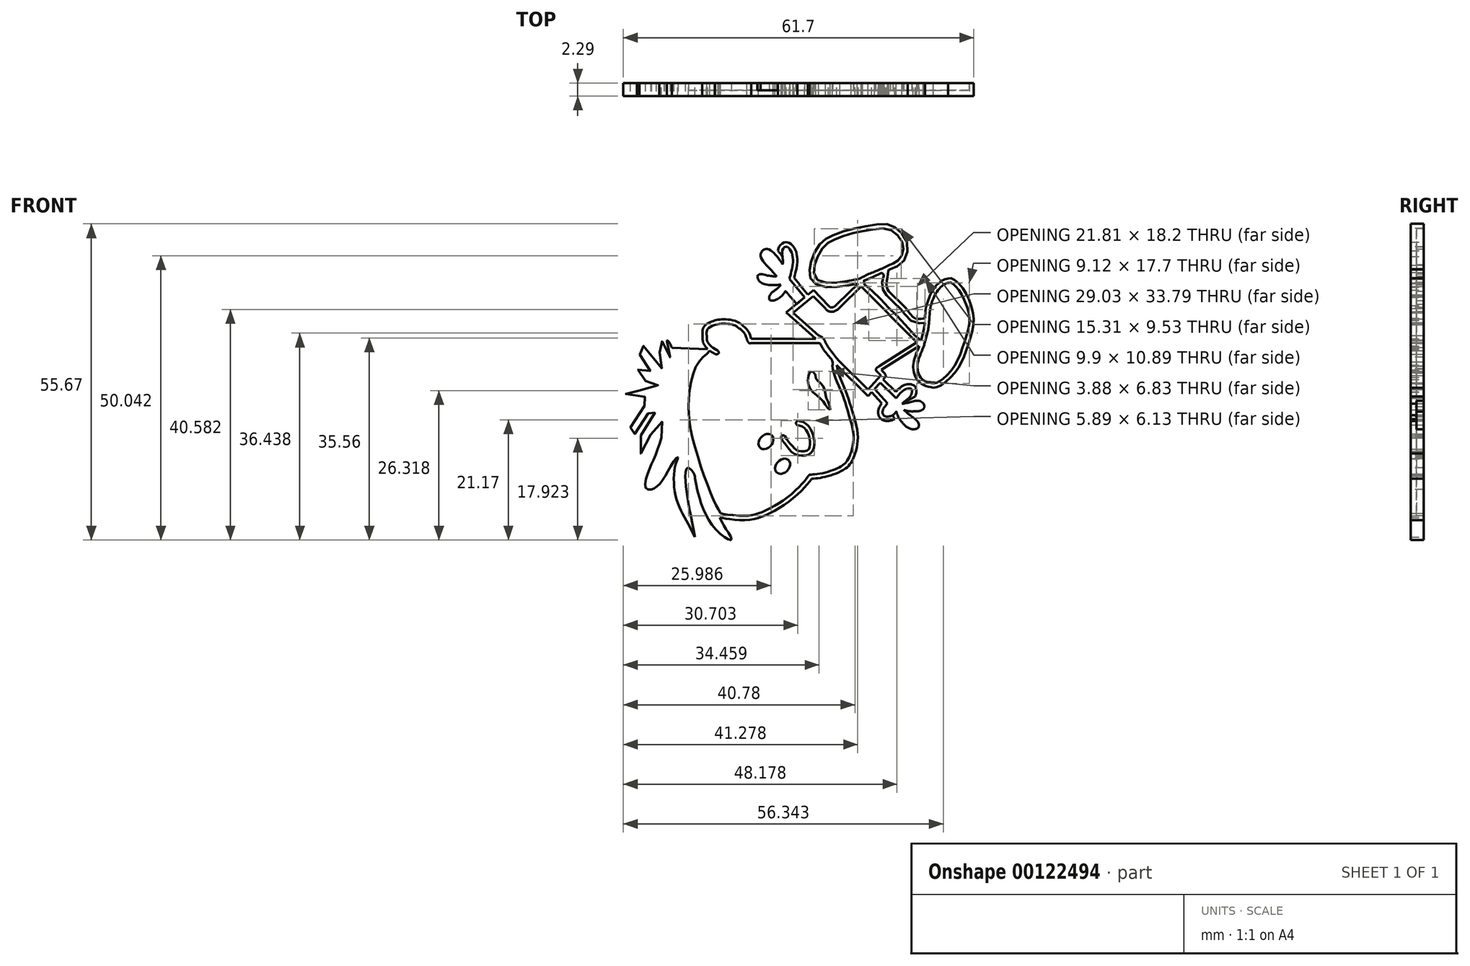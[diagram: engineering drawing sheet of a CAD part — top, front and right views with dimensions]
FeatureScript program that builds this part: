
annotation { "Feature Type Name" : "Feature", "Feature Type Description" : "" }
export const myFeature = defineFeature(function(context is Context, id is Id, definition is map)
    precondition{}
    {
        {
            var Q0;
            Q0=qCreatedBy(makeId("Front.planeOp"),FACE);
            var sketch = newSketch(context, id + "F0", { "sketchPlane" : qUnion([Q0])});
            skLineSegment(sketch, "E0.bottom", {"start": v(-35.67, 28.6) * mm, "end": v(40.53, 28.6) * mm});
            skLineSegment(sketch, "E0.top", {"start": v(-35.67, -29.82) * mm, "end": v(40.53, -29.82) * mm});
            skLineSegment(sketch, "E0.left", {"start": v(-35.67, 28.6) * mm, "end": v(-35.67, -29.82) * mm});
            skLineSegment(sketch, "E0.right", {"start": v(40.53, 28.6) * mm, "end": v(40.53, -29.82) * mm});
            skFitSpline(sketch, "E1", {"points": [v(2.5, -18.66) * mm, v(1.1, -20.33) * mm, v(-2.3, -23.23) * mm, v(-5.73, -25.1) * mm, v(-8.32, -25.86) * mm, v(-12.02, -25.75) * mm, v(-13.66, -25.48) * mm], "startDerivative": vector(-8.55, -11.05) * mm, "endDerivative": vector(-11.53, 2.21) * mm});
            skFitSpline(sketch, "E2.0", {"points": [v(1.9, -18.2) * mm, v(1.73, -18.42) * mm, v(1.47, -18.76) * mm, v(1.08, -19.22) * mm, v(0.75, -19.6) * mm, v(0.38, -19.99) * mm, v(-0.2, -20.56) * mm, v(-1.04, -21.32) * mm, v(-1.96, -22.06) * mm, v(-2.71, -22.6) * mm, v(-3.46, -23.1) * mm, v(-4.4, -23.63) * mm, v(-5.3, -24.08) * mm, v(-6, -24.39) * mm, v(-6.48, -24.6) * mm, v(-6.93, -24.77) * mm, v(-7.37, -24.91) * mm, v(-7.83, -25.02) * mm, v(-8.32, -25.1) * mm, v(-8.88, -25.15) * mm, v(-9.7, -25.16) * mm, v(-10.78, -25.12) * mm, v(-11.96, -25) * mm, v(-12.81, -24.87) * mm, v(-13.28, -24.78) * mm, v(-13.52, -24.73) * mm]});
            skFitSpline(sketch, "E3", {"points": [v(-13.66, -25.48) * mm, v(-12.8, -27.15) * mm, v(-11.63, -29.37) * mm, v(-14.37, -27.58) * mm, v(-17.37, -21.62) * mm, v(-18.02, -18.58) * mm], "startDerivative": vector(4.17, -9.52) * mm, "endDerivative": vector(-2.4, 14.14) * mm});
            skFitSpline(sketch, "E4", {"points": [v(-18.02, -18.58) * mm, v(-18.37, -17.5) * mm, v(-19.41, -16.75) * mm, v(-19.59, -20.54) * mm, v(-18.72, -25.45) * mm, v(-18.02, -28.89) * mm], "startDerivative": vector(-1.13, 8.11) * mm, "endDerivative": vector(2.94, -14.74) * mm});
            skFitSpline(sketch, "E5", {"points": [v(-18.02, -28.89) * mm, v(-19.98, -25.28) * mm, v(-21.6, -21.1) * mm, v(-21.55, -16.45) * mm, v(-21.07, -15.14) * mm], "startDerivative": vector(-7.28, 13.23) * mm, "endDerivative": vector(3.3, 6.7) * mm});
            skFitSpline(sketch, "E6", {"points": [v(-21.07, -15.14) * mm, v(-21.07, -14.86) * mm, v(-21.75, -15.5) * mm, v(-23.44, -18.41) * mm, v(-24.73, -20) * mm, v(-25.83, -20.55) * mm, v(-26.73, -20.25) * mm, v(-26.38, -17.7) * mm, v(-25.28, -15.14) * mm, v(-23.94, -11.4) * mm], "startDerivative": vector(1.52, 8.73) * mm, "endDerivative": vector(8.18, 24.32) * mm});
            skFitSpline(sketch, "E7", {"points": [v(-23.94, -11.4) * mm, v(-23.54, -10.35) * mm, v(-23.94, -8.56) * mm, v(-25.18, -9.9) * mm, v(-26.38, -11.85) * mm, v(-27.63, -14.2) * mm, v(-27.98, -13.2) * mm, v(-26.83, -9.5) * mm, v(-24.93, -6.56) * mm, v(-25.13, -6) * mm, v(-26.78, -7.86) * mm, v(-28.63, -10.7) * mm, v(-29.28, -11.4) * mm, v(-29.38, -9.5) * mm, v(-27.33, -6.16) * mm, v(-25.73, -4.36) * mm, v(-27.3, -4.27) * mm, v(-29.38, -4.07) * mm, v(-30.66, -3.33) * mm, v(-27.98, -3.13) * mm, v(-25.43, -2.66) * mm, v(-24.38, -1.85) * mm, v(-26.03, -1.65) * mm, v(-27.7, -0.51) * mm, v(-28.24, 0.56) * mm, v(-26.9, 0.1) * mm, v(-25.9, 0.02) * mm, v(-26.9, 1.77) * mm, v(-27.78, 3.44) * mm, v(-27.57, 5.32) * mm, v(-26.23, 3.18) * mm, v(-23.53, 0.79) * mm, v(-24.18, 3.23) * mm, v(-24.21, 4.8) * mm, v(-23.94, 5.7) * mm, v(-23.47, 4.16) * mm, v(-22.45, 2.75) * mm, v(-22.6, 3.68) * mm, v(-22.96, 5.39) * mm], "startDerivative": vector(25.66, 39.72) * mm, "endDerivative": vector(-0.87, 29.22) * mm});
            skFitSpline(sketch, "E8", {"points": [v(-14.36, 3.25) * mm, v(-15.42, 3.88) * mm, v(-16.03, 4.43) * mm, v(-16.57, 5.22) * mm, v(-16.72, 6.25) * mm, v(-16.63, 7.79) * mm, v(-15.75, 8.76) * mm, v(-14.54, 9.24) * mm], "startDerivative": vector(-7.8, 4.34) * mm, "endDerivative": vector(8.24, 2.58) * mm});
            skFitSpline(sketch, "E9", {"points": [v(-14.54, 9.24) * mm, v(-13.74, 9.38) * mm, v(-12.47, 9.4) * mm, v(-10.85, 9.1) * mm, v(-9.37, 8.1) * mm, v(-8.6, 7.23) * mm, v(-8.27, 6.45) * mm, v(-8.15, 6) * mm], "startDerivative": vector(6.15, 1.3) * mm, "endDerivative": vector(1.17, -4.4) * mm});
            skFitSpline(sketch, "E10", {"points": [v(-13.52, -24.73) * mm, v(-15.03, -21.77) * mm, v(-18.32, -12.1) * mm, v(-19.17, -4.98) * mm, v(-17.47, 1.8) * mm, v(-15.42, 3.88) * mm], "startDerivative": vector(-9.54, 15.92) * mm, "endDerivative": vector(10.17, 11.75) * mm});
            skFitSpline(sketch, "E11", {"points": [v(-22.96, 5.39) * mm, v(-22.96, 5.68) * mm, v(-22.7, 5.55) * mm, v(-22.12, 4.42) * mm], "startDerivative": vector(-0.27, 1.56) * mm, "endDerivative": vector(1.09, -2.65) * mm});
            skLineSegment(sketch, "E12", {"start": v(-22.12, 4.42) * mm, "end": v(-15.8, 4.2) * mm});
            skFitSpline(sketch, "E13.0", {"points": [v(-14.38, 8.5) * mm, v(-14.26, 8.52) * mm, v(-14.01, 8.58) * mm, v(-13.66, 8.63) * mm, v(-13.23, 8.66) * mm, v(-12.74, 8.66) * mm, v(-12.2, 8.64) * mm, v(-11.78, 8.59) * mm, v(-11.47, 8.51) * mm, v(-11.24, 8.44) * mm, v(-11.03, 8.35) * mm, v(-10.8, 8.24) * mm, v(-10.58, 8.1) * mm, v(-10.36, 7.94) * mm, v(-10.14, 7.76) * mm, v(-9.94, 7.59) * mm, v(-9.74, 7.41) * mm, v(-9.52, 7.2) * mm, v(-9.36, 7.01) * mm, v(-9.25, 6.85) * mm, v(-9.18, 6.71) * mm, v(-9.11, 6.56) * mm, v(-9.06, 6.4) * mm, v(-9, 6.24) * mm, v(-8.95, 6.03) * mm, v(-8.91, 5.9) * mm, v(-8.89, 5.81) * mm]});
            skFitSpline(sketch, "E13.1", {"points": [v(-14, 3.91) * mm, v(-14.15, 4) * mm, v(-14.47, 4.18) * mm, v(-14.81, 4.39) * mm, v(-15.02, 4.53) * mm, v(-15.2, 4.67) * mm, v(-15.35, 4.82) * mm, v(-15.53, 5.01) * mm, v(-15.65, 5.16) * mm, v(-15.76, 5.3) * mm, v(-15.82, 5.4) * mm, v(-15.86, 5.48) * mm, v(-15.88, 5.54) * mm, v(-15.9, 5.64) * mm, v(-15.93, 5.8) * mm, v(-15.94, 5.98) * mm, v(-15.95, 6.14) * mm, v(-15.96, 6.28) * mm, v(-15.97, 6.42) * mm, v(-15.98, 6.61) * mm, v(-16, 6.84) * mm, v(-15.99, 7.1) * mm, v(-15.97, 7.32) * mm, v(-15.94, 7.47) * mm, v(-15.9, 7.55) * mm, v(-15.87, 7.63) * mm, v(-15.8, 7.74) * mm, v(-15.7, 7.86) * mm, v(-15.51, 8.02) * mm, v(-15.22, 8.2) * mm, v(-14.81, 8.36) * mm, v(-14.49, 8.46) * mm, v(-14.32, 8.52) * mm]});
            skFitSpline(sketch, "E14", {"points": [v(-14.36, 3.25) * mm, v(-13.86, 3.45) * mm, v(-14, 3.91) * mm], "startDerivative": vector(1.3, 0.25) * mm, "endDerivative": vector(-0.58, 1.09) * mm});
            skLineSegment(sketch, "E15", {"start": v(-8.15, 6) * mm, "end": v(3.2, 6) * mm});
            skLineSegment(sketch, "E16.0", {"start": v(-8.15, 5.25) * mm, "end": v(3.2, 5.25) * mm});
            skFitSpline(sketch, "E17", {"points": [v(-8.15, 5.25) * mm, v(-8.51, 5.25) * mm, v(-8.89, 5.81) * mm], "startDerivative": vector(-0.9, -0.2) * mm, "endDerivative": vector(-0.59, 1.26) * mm});
            skFitSpline(sketch, "E18", {"points": [v(2.5, -18.66) * mm, v(4.7, -18.35) * mm, v(7.9, -17.2) * mm, v(9.41, -15.84) * mm, v(10.17, -14.2) * mm], "startDerivative": vector(8.36, 0.78) * mm, "endDerivative": vector(2.95, 7.75) * mm});
            skFitSpline(sketch, "E19", {"points": [v(10.17, -14.2) * mm, v(10.55, -12.5) * mm, v(10.55, -10.21) * mm, v(9.56, -6.45) * mm, v(8.65, -3.6) * mm, v(7.33, -0.37) * mm, v(6.91, 1.37) * mm], "startDerivative": vector(3.2, 12.34) * mm, "endDerivative": vector(-2.07, 11.63) * mm});
            skFitSpline(sketch, "E20.0", {"points": [v(2.44, -17.9) * mm, v(2.78, -17.87) * mm, v(3.46, -17.8) * mm, v(4.55, -17.62) * mm, v(5.67, -17.31) * mm, v(6.54, -17) * mm, v(7.15, -16.74) * mm, v(7.67, -16.47) * mm, v(8.07, -16.19) * mm, v(8.4, -15.9) * mm, v(8.67, -15.58) * mm, v(8.9, -15.24) * mm, v(9.16, -14.72) * mm, v(9.34, -14.26) * mm, v(9.46, -13.93) * mm]});
            skFitSpline(sketch, "E21", {"points": [v(1.9, -18.2) * mm, v(2.11, -17.95) * mm, v(2.44, -17.9) * mm], "startDerivative": vector(0.36, 0.59) * mm, "endDerivative": vector(0.7, 0) * mm});
            skFitSpline(sketch, "E22.0", {"points": [v(9.44, -14.01) * mm, v(9.5, -13.75) * mm, v(9.63, -13.25) * mm, v(9.79, -12.5) * mm, v(9.88, -11.76) * mm, v(9.89, -11.09) * mm, v(9.83, -10.48) * mm, v(9.72, -9.82) * mm, v(9.5, -8.87) * mm, v(9.14, -7.68) * mm, v(8.79, -6.53) * mm, v(8.5, -5.52) * mm, v(8.2, -4.59) * mm, v(7.85, -3.63) * mm, v(7.39, -2.54) * mm, v(7, -1.62) * mm, v(6.72, -0.92) * mm, v(6.48, -0.25) * mm, v(6.3, 0.5) * mm, v(6.2, 1) * mm, v(6.16, 1.24) * mm]});
            skFitSpline(sketch, "E23", {"points": [v(-0.07, -9.19) * mm, v(0.93, -9.47) * mm, v(1.73, -10.4) * mm, v(2.17, -11.84) * mm, v(2.17, -12.96) * mm, v(1.8, -13.6) * mm, v(0.54, -13.8) * mm, v(-0.29, -13.5) * mm, v(-1.22, -12.51) * mm, v(-1.89, -11.65) * mm, v(-2.24, -11.07) * mm], "startDerivative": vector(10.6, -1.7) * mm, "endDerivative": vector(-4.01, 7.06) * mm});
            skFitSpline(sketch, "E24.0", {"points": [v(0.06, -8.43) * mm, v(0.17, -8.45) * mm, v(0.4, -8.49) * mm, v(0.74, -8.57) * mm, v(1.03, -8.67) * mm, v(1.25, -8.78) * mm, v(1.47, -8.92) * mm, v(1.73, -9.12) * mm, v(2.01, -9.42) * mm, v(2.28, -9.82) * mm, v(2.5, -10.24) * mm, v(2.68, -10.68) * mm, v(2.81, -11.13) * mm, v(2.9, -11.58) * mm, v(2.97, -12.02) * mm, v(3, -12.44) * mm, v(2.97, -12.8) * mm, v(2.93, -13.06) * mm, v(2.87, -13.33) * mm, v(2.76, -13.64) * mm, v(2.55, -13.95) * mm, v(2.33, -14.16) * mm, v(2.07, -14.33) * mm, v(1.8, -14.43) * mm, v(1.55, -14.5) * mm, v(1.22, -14.55) * mm, v(0.9, -14.57) * mm, v(0.59, -14.56) * mm, v(0.3, -14.54) * mm, v(-0.07, -14.47) * mm, v(-0.5, -14.3) * mm, v(-0.88, -14.02) * mm, v(-1.2, -13.7) * mm, v(-1.5, -13.38) * mm, v(-1.75, -13.06) * mm, v(-2, -12.77) * mm, v(-2.22, -12.49) * mm, v(-2.43, -12.21) * mm, v(-2.68, -11.84) * mm, v(-2.82, -11.6) * mm, v(-2.9, -11.45) * mm]});
            skFitSpline(sketch, "E25", {"points": [v(-2.9, -11.45) * mm, v(-2.72, -11.01) * mm, v(-2.24, -11.07) * mm], "startDerivative": vector(0.22, 1.13) * mm, "endDerivative": vector(1.1, -0.37) * mm});
            skFitSpline(sketch, "E26", {"points": [v(-0.07, -9.19) * mm, v(-0.29, -8.79) * mm, v(0.06, -8.43) * mm], "startDerivative": vector(-0.73, 0.84) * mm, "endDerivative": vector(0.96, 0.67) * mm});
            skEllipse(sketch, "E27", {"center": v(-5.56, -12.08) * mm, "majorRadius": 1.5 * mm, "minorRadius": 1.13 * mm, "majorAxis": v(0.68, 0.73)});
            skEllipse(sketch, "E28", {"center": v(-2.61, -16.43) * mm, "majorRadius": 1.5 * mm, "minorRadius": 1.13 * mm, "majorAxis": v(0.68, 0.73)});
            skFitSpline(sketch, "E29", {"points": [v(5.74, -6.52) * mm, v(4.98, -5.77) * mm, v(4.5, -4.94) * mm, v(3.18, -3.8) * mm, v(2.09, -2.57) * mm, v(1.86, -1.17) * mm, v(2.31, 0.3) * mm, v(3.1, -0.16) * mm, v(3.25, -1.02) * mm, v(3.9, -1.63) * mm, v(4.72, -2.72) * mm, v(4.98, -4.03) * mm, v(5.4, -5.16) * mm, v(5.74, -6.52) * mm]});
            skLineSegment(sketch, "E30", {"start": v(6.91, 1.37) * mm, "end": v(12.43, -4.08) * mm});
            skFitSpline(sketch, "E31", {"points": [v(15.43, -0.8) * mm, v(15.55, -0.63) * mm, v(15.43, -0.21) * mm, v(14.79, 0.53) * mm], "startDerivative": vector(0.72, 0.68) * mm, "endDerivative": vector(-1.54, 1.65) * mm});
            skLineSegment(sketch, "E32", {"start": v(14.79, 0.53) * mm, "end": v(21.47, 4.75) * mm});
            skLineSegment(sketch, "E33", {"start": v(3.2, 6) * mm, "end": v(-1.96, 10.62) * mm});
            skLineSegment(sketch, "E34", {"start": v(-1.96, 10.62) * mm, "end": v(2.82, 14.57) * mm});
            skLineSegment(sketch, "E35", {"start": v(2.82, 14.57) * mm, "end": v(5.46, 11.87) * mm});
            skFitSpline(sketch, "E36", {"points": [v(5.46, 11.87) * mm, v(5.72, 11.59) * mm, v(6.25, 11.56) * mm, v(7.09, 12.2) * mm], "startDerivative": vector(0.83, -1.22) * mm, "endDerivative": vector(1.93, 1.9) * mm});
            skLineSegment(sketch, "E37", {"start": v(7.09, 12.2) * mm, "end": v(10.7, 15.76) * mm});
            skFitSpline(sketch, "E38", {"points": [v(6.16, 1.24) * mm, v(6.16, 2.04) * mm, v(5.3, 3.2) * mm, v(4.31, 4.55) * mm, v(3.95, 5.17) * mm, v(3.2, 5.25) * mm], "startDerivative": vector(0.79, 4.51) * mm, "endDerivative": vector(-5.08, -0.36) * mm});
            skFitSpline(sketch, "E39", {"points": [v(21.47, 4.75) * mm, v(20.57, 2.37) * mm, v(20.41, 0.46) * mm, v(21.47, -1.69) * mm, v(23.9, -2.6) * mm], "startDerivative": vector(-4.04, -9.6) * mm, "endDerivative": vector(10.28, -2.2) * mm});
            skFitSpline(sketch, "E40", {"points": [v(23.9, -2.6) * mm, v(25.03, -2.3) * mm, v(27.01, -0.78) * mm, v(28.68, 1.51) * mm, v(29.73, 4) * mm, v(30.74, 7.22) * mm, v(31.01, 9.9) * mm, v(30.12, 13.04) * mm, v(28.65, 15.5) * mm, v(27.17, 16.62) * mm, v(26.5, 16.62) * mm], "startDerivative": vector(14.92, 2.44) * mm, "endDerivative": vector(-11.36, -2.14) * mm});
            skFitSpline(sketch, "E41", {"points": [v(26.5, 16.62) * mm, v(25.51, 16.29) * mm, v(24.13, 15) * mm, v(23.26, 13.46) * mm, v(22.69, 11.7) * mm, v(22.46, 9.63) * mm], "startDerivative": vector(-6.17, -1.27) * mm, "endDerivative": vector(-0.6, -9.52) * mm});
            skFitSpline(sketch, "E42.0", {"points": [v(22.16, 4.46) * mm, v(22, 4.06) * mm, v(21.75, 3.47) * mm, v(21.47, 2.74) * mm, v(21.3, 2.23) * mm, v(21.19, 1.77) * mm, v(21.12, 1.34) * mm, v(21.11, 0.92) * mm, v(21.16, 0.47) * mm, v(21.29, -0.02) * mm, v(21.48, -0.5) * mm, v(21.7, -0.83) * mm, v(21.88, -1.04) * mm, v(22.03, -1.17) * mm, v(22.2, -1.3) * mm, v(22.46, -1.43) * mm, v(22.86, -1.59) * mm, v(23.43, -1.73) * mm, v(23.85, -1.82) * mm, v(24.06, -1.87) * mm]});
            skFitSpline(sketch, "E43.0", {"points": [v(26.66, 15.87) * mm, v(26.53, 15.85) * mm, v(26.3, 15.8) * mm, v(26.08, 15.72) * mm, v(25.9, 15.63) * mm, v(25.74, 15.53) * mm, v(25.57, 15.4) * mm, v(25.33, 15.2) * mm, v(25.02, 14.9) * mm, v(24.7, 14.49) * mm, v(24.43, 14.1) * mm, v(24.2, 13.67) * mm, v(24, 13.23) * mm, v(23.73, 12.59) * mm, v(23.51, 11.94) * mm, v(23.38, 11.28) * mm, v(23.28, 10.56) * mm, v(23.25, 9.98) * mm, v(23.22, 9.59) * mm]});
            skFitSpline(sketch, "E43.1", {"points": [v(23.78, -1.85) * mm, v(23.94, -1.83) * mm, v(24.15, -1.8) * mm, v(24.4, -1.73) * mm, v(24.6, -1.66) * mm, v(24.8, -1.57) * mm, v(25.04, -1.43) * mm, v(25.3, -1.26) * mm, v(25.67, -1) * mm, v(26.14, -0.59) * mm, v(26.67, -0.05) * mm, v(27.15, 0.53) * mm, v(27.58, 1.13) * mm, v(27.96, 1.76) * mm, v(28.39, 2.6) * mm, v(28.74, 3.49) * mm, v(29.11, 4.52) * mm, v(29.4, 5.33) * mm, v(29.66, 6.17) * mm, v(29.9, 6.99) * mm, v(30.1, 7.76) * mm, v(30.23, 8.47) * mm, v(30.3, 9.14) * mm, v(30.27, 9.81) * mm, v(30.16, 10.55) * mm, v(29.96, 11.32) * mm, v(29.69, 12.11) * mm, v(29.37, 12.88) * mm, v(29.03, 13.59) * mm, v(28.66, 14.22) * mm, v(28.32, 14.7) * mm, v(28.03, 15.04) * mm, v(27.8, 15.28) * mm, v(27.57, 15.5) * mm, v(27.35, 15.67) * mm, v(27.15, 15.8) * mm, v(27.02, 15.86) * mm, v(26.95, 15.89) * mm, v(26.91, 15.9) * mm, v(26.88, 15.9) * mm, v(26.8, 15.9) * mm, v(26.7, 15.88) * mm, v(26.65, 15.87) * mm]});
            skFitSpline(sketch, "E44", {"points": [v(22.46, 9.63) * mm, v(21.82, 9.53) * mm, v(20.66, 9.63) * mm, v(19.18, 11.25) * mm, v(17.62, 12.85) * mm, v(16.42, 14.01) * mm, v(15.86, 14.65) * mm, v(15.7, 15.7) * mm, v(15.94, 17.5) * mm, v(16.08, 18.18) * mm], "startDerivative": vector(-7.76, -0.9) * mm, "endDerivative": vector(1.85, 7.1) * mm});
            skFitSpline(sketch, "E45", {"points": [v(22.16, 4.46) * mm, v(22.4, 5.22) * mm, v(22.77, 6.54) * mm, v(23.08, 8.01) * mm, v(23.22, 9.59) * mm], "startDerivative": vector(1.02, 3.44) * mm, "endDerivative": vector(0.38, 5.72) * mm});
            skPoint(sketch, "E46", {"position": v(16.08, 18.94) * mm});
            skFitSpline(sketch, "E47", {"points": [v(16.08, 18.94) * mm, v(16.6, 19.17) * mm, v(17.33, 19.51) * mm, v(17.92, 19.97) * mm, v(18.48, 20.98) * mm, v(18.66, 22.2) * mm, v(18.18, 23.55) * mm, v(16.85, 24.9) * mm, v(15.26, 25.47) * mm, v(12.23, 25.1) * mm, v(9.96, 24.63) * mm, v(7.59, 23.94) * mm, v(5.86, 23.16) * mm, v(4.6, 22.22) * mm, v(3.4, 20.14) * mm, v(2.94, 18.54) * mm, v(3.13, 16.72) * mm, v(5.15, 15.88) * mm, v(7.91, 16.04) * mm, v(10.53, 16.5) * mm], "startDerivative": vector(16.63, 6.8) * mm, "endDerivative": vector(38.76, 9.66) * mm});
            skFitSpline(sketch, "E48.0", {"points": [v(16.37, 18.24) * mm, v(16.55, 18.3) * mm, v(16.82, 18.42) * mm, v(17.27, 18.62) * mm, v(17.62, 18.8) * mm, v(17.98, 19) * mm, v(18.35, 19.3) * mm, v(18.68, 19.69) * mm, v(18.95, 20.13) * mm, v(19.18, 20.62) * mm, v(19.34, 21.14) * mm, v(19.43, 21.68) * mm, v(19.43, 22.25) * mm, v(19.34, 22.82) * mm, v(19.15, 23.38) * mm, v(18.86, 23.92) * mm, v(18.49, 24.43) * mm, v(18.06, 24.9) * mm, v(17.66, 25.24) * mm, v(17.34, 25.49) * mm, v(17, 25.71) * mm, v(16.56, 25.96) * mm, v(16.05, 26.12) * mm, v(15.6, 26.2) * mm, v(15.14, 26.24) * mm, v(14.54, 26.23) * mm, v(13.8, 26.15) * mm, v(13.05, 26.03) * mm, v(12.34, 25.9) * mm, v(11.7, 25.77) * mm, v(10.91, 25.61) * mm, v(10.17, 25.46) * mm, v(9.37, 25.27) * mm, v(8.54, 25.06) * mm, v(7.7, 24.8) * mm, v(6.93, 24.51) * mm, v(6.39, 24.28) * mm, v(5.97, 24.08) * mm, v(5.66, 23.92) * mm, v(5.36, 23.76) * mm, v(4.97, 23.54) * mm, v(4.58, 23.26) * mm, v(4.27, 22.99) * mm, v(4.04, 22.75) * mm, v(3.83, 22.5) * mm, v(3.56, 22.12) * mm, v(3.26, 21.63) * mm, v(2.95, 21.02) * mm, v(2.68, 20.44) * mm, v(2.48, 19.9) * mm, v(2.32, 19.38) * mm, v(2.23, 18.94) * mm, v(2.17, 18.56) * mm, v(2.12, 18.15) * mm, v(2.1, 17.7) * mm, v(2.14, 17.23) * mm, v(2.22, 16.86) * mm, v(2.37, 16.5) * mm, v(2.6, 16.13) * mm, v(2.9, 15.85) * mm, v(3.34, 15.56) * mm, v(3.92, 15.32) * mm, v(4.66, 15.15) * mm, v(5.4, 15.08) * mm, v(6.11, 15.08) * mm, v(6.8, 15.13) * mm, v(7.48, 15.21) * mm, v(8.13, 15.3) * mm, v(8.78, 15.4) * mm, v(9.64, 15.53) * mm, v(10.3, 15.66) * mm, v(10.72, 15.76) * mm]});
            skFitSpline(sketch, "E49", {"points": [v(16.37, 18.24) * mm, v(16.08, 18.18) * mm], "startDerivative": vector(-0.29, -0.06) * mm, "endDerivative": vector(-0.29, -0.06) * mm});
            skFitSpline(sketch, "E50", {"points": [v(10.53, 16.5) * mm, v(12.05, 17.19) * mm, v(14.1, 18.04) * mm, v(16.08, 18.94) * mm], "startDerivative": vector(5.38, 1.13) * mm, "endDerivative": vector(5.42, 2.95) * mm});
            skLineSegment(sketch, "E51.0", {"start": v(14.38, 1.18) * mm, "end": v(21.03, 5.37) * mm});
            skLineSegment(sketch, "E52.1", {"start": v(12.4, -2.96) * mm, "end": v(14.68, -0.48) * mm});
            skLineSegment(sketch, "E52.2", {"start": v(7.46, 1.92) * mm, "end": v(12.4, -2.96) * mm});
            skPoint(sketch, "E53", {"position": v(14.24, 0.02) * mm});
            skFitSpline(sketch, "E54", {"points": [v(14.68, -0.48) * mm, v(14.51, -0.27) * mm, v(14.24, 0.02) * mm], "startDerivative": vector(-0.34, 0.46) * mm, "endDerivative": vector(-0.53, 0.53) * mm});
            skLineSegment(sketch, "E55.0", {"start": v(2.76, 13.53) * mm, "end": v(4.94, 11.3) * mm});
            skLineSegment(sketch, "E55.1", {"start": v(-0.79, 10.6) * mm, "end": v(2.76, 13.53) * mm});
            skLineSegment(sketch, "E55.2", {"start": v(3.7, 6.59) * mm, "end": v(-0.79, 10.6) * mm});
            skLineSegment(sketch, "E56.0", {"start": v(7.62, 11.67) * mm, "end": v(11.24, 15.24) * mm});
            skFitSpline(sketch, "E56.1", {"points": [v(4.84, 11.44) * mm, v(4.86, 11.42) * mm, v(4.9, 11.36) * mm, v(5, 11.23) * mm, v(5.12, 11.1) * mm, v(5.28, 10.97) * mm, v(5.43, 10.9) * mm, v(5.58, 10.83) * mm, v(5.77, 10.78) * mm, v(6, 10.76) * mm, v(6.25, 10.78) * mm, v(6.49, 10.84) * mm, v(6.71, 10.94) * mm, v(6.9, 11.05) * mm, v(7.12, 11.21) * mm, v(7.36, 11.42) * mm, v(7.53, 11.6) * mm, v(7.62, 11.67) * mm]});
            skLineSegment(sketch, "E57", {"start": v(21.03, 5.37) * mm, "end": v(11.24, 15.24) * mm});
            skFitSpline(sketch, "E58", {"points": [v(3.7, 6.59) * mm, v(4.44, 6.19) * mm, v(4.96, 5.31) * mm, v(5.56, 4.3) * mm, v(6.82, 2.72) * mm, v(7.46, 1.92) * mm], "startDerivative": vector(4.71, -1.76) * mm, "endDerivative": vector(3, -3.82) * mm});
            skFitSpline(sketch, "E59", {"points": [v(14.24, 0.02) * mm, v(13.8, 0.58) * mm, v(14.38, 1.18) * mm], "startDerivative": vector(-1.42, 1.19) * mm, "endDerivative": vector(1.67, 1.13) * mm});
            skFitSpline(sketch, "E60", {"points": [v(13.59, -2.81) * mm, v(15.84, -5.33) * mm], "startDerivative": vector(2.25, -2.52) * mm, "endDerivative": vector(2.25, -2.52) * mm});
            skFitSpline(sketch, "E61", {"points": [v(15.84, -5.33) * mm, v(15.53, -5.75) * mm, v(15.07, -6.45) * mm, v(15.1, -7.38) * mm, v(15.84, -7.7) * mm, v(16.93, -7.34) * mm, v(17.39, -6.76) * mm], "startDerivative": vector(-2.1, -3.07) * mm, "endDerivative": vector(2.28, 3.92) * mm});
            skFitSpline(sketch, "E62", {"points": [v(17.39, -6.76) * mm, v(17.82, -7.85) * mm, v(18.55, -8.85) * mm, v(19.79, -9.82) * mm, v(21.18, -9.7) * mm, v(21.3, -8.81) * mm, v(20.37, -7.85) * mm, v(18.7, -6.53) * mm], "startDerivative": vector(2.78, -8.47) * mm, "endDerivative": vector(-9.72, 7.75) * mm});
            skFitSpline(sketch, "E63", {"points": [v(18.7, -6.53) * mm, v(19.68, -6.76) * mm, v(20.9, -6.76) * mm, v(21.98, -6.53) * mm, v(22.36, -5.76) * mm, v(21.41, -4.92) * mm, v(19.96, -5.12) * mm, v(18.42, -5.43) * mm], "startDerivative": vector(7.2, -2.18) * mm, "endDerivative": vector(-9.43, -1.54) * mm});
            skFitSpline(sketch, "E64", {"points": [v(18.42, -5.43) * mm, v(19.09, -4.87) * mm, v(19.98, -3.97) * mm, v(20.09, -2.88) * mm, v(19.22, -2.82) * mm, v(18.04, -3.64) * mm, v(17.4, -4.46) * mm], "startDerivative": vector(4.15, 3.68) * mm, "endDerivative": vector(-3.44, -4.99) * mm});
            skFitSpline(sketch, "E65", {"points": [v(17.4, -4.46) * mm, v(14.6, -1.7) * mm], "startDerivative": vector(-2.8, 2.75) * mm, "endDerivative": vector(-2.8, 2.75) * mm});
            skFitSpline(sketch, "E66.0", {"points": [v(15.2, -4.9) * mm, v(15.16, -4.96) * mm, v(15.1, -5.05) * mm, v(15.02, -5.16) * mm, v(14.97, -5.23) * mm, v(14.92, -5.29) * mm, v(14.86, -5.36) * mm, v(14.78, -5.46) * mm, v(14.66, -5.61) * mm, v(14.53, -5.8) * mm, v(14.41, -6.01) * mm, v(14.31, -6.27) * mm, v(14.25, -6.54) * mm, v(14.21, -6.82) * mm, v(14.22, -7.1) * mm, v(14.27, -7.4) * mm, v(14.38, -7.7) * mm, v(14.59, -7.99) * mm, v(14.85, -8.2) * mm, v(15.13, -8.34) * mm, v(15.4, -8.42) * mm, v(15.77, -8.47) * mm, v(16.21, -8.44) * mm, v(16.63, -8.34) * mm, v(16.95, -8.21) * mm, v(17.18, -8.1) * mm, v(17.4, -7.95) * mm, v(17.67, -7.72) * mm, v(17.9, -7.43) * mm, v(18, -7.23) * mm, v(18.05, -7.15) * mm]});
            skFitSpline(sketch, "E67.0", {"points": [v(16.66, -7) * mm, v(16.72, -7.18) * mm, v(16.81, -7.45) * mm, v(16.97, -7.84) * mm, v(17.1, -8.14) * mm, v(17.27, -8.44) * mm, v(17.51, -8.8) * mm, v(17.78, -9.13) * mm, v(18.06, -9.46) * mm, v(18.3, -9.72) * mm, v(18.6, -9.99) * mm, v(18.92, -10.24) * mm, v(19.32, -10.47) * mm, v(19.78, -10.63) * mm, v(20.25, -10.7) * mm, v(20.64, -10.7) * mm, v(20.96, -10.64) * mm, v(21.2, -10.57) * mm, v(21.44, -10.47) * mm, v(21.63, -10.33) * mm, v(21.78, -10.2) * mm, v(21.9, -10.04) * mm, v(22.02, -9.84) * mm, v(22.1, -9.59) * mm, v(22.16, -9.26) * mm, v(22.13, -8.94) * mm, v(22.06, -8.64) * mm, v(21.94, -8.36) * mm, v(21.74, -8.05) * mm, v(21.47, -7.76) * mm, v(21.2, -7.52) * mm, v(20.92, -7.3) * mm, v(20.65, -7.1) * mm, v(20.28, -6.8) * mm, v(19.79, -6.42) * mm, v(19.38, -6.1) * mm, v(19.18, -5.93) * mm]});
            skFitSpline(sketch, "E68.0", {"points": [v(18.48, -7.26) * mm, v(18.63, -7.3) * mm, v(18.87, -7.38) * mm, v(19.24, -7.47) * mm, v(19.53, -7.52) * mm, v(19.85, -7.55) * mm, v(20.15, -7.55) * mm, v(20.44, -7.55) * mm, v(20.68, -7.54) * mm, v(20.87, -7.53) * mm, v(21.04, -7.52) * mm, v(21.29, -7.5) * mm, v(21.61, -7.47) * mm, v(21.96, -7.39) * mm, v(22.27, -7.25) * mm, v(22.51, -7.1) * mm, v(22.73, -6.9) * mm, v(22.96, -6.6) * mm, v(23.1, -6.24) * mm, v(23.15, -5.9) * mm, v(23.12, -5.63) * mm, v(23.05, -5.37) * mm, v(22.94, -5.15) * mm, v(22.8, -4.95) * mm, v(22.6, -4.72) * mm, v(22.32, -4.49) * mm, v(21.99, -4.3) * mm, v(21.7, -4.2) * mm, v(21.4, -4.13) * mm, v(21.02, -4.1) * mm, v(20.63, -4.15) * mm, v(20.28, -4.24) * mm, v(20.02, -4.3) * mm, v(19.83, -4.36) * mm, v(19.65, -4.41) * mm, v(19.43, -4.47) * mm, v(19.16, -4.52) * mm, v(18.79, -4.6) * mm, v(18.5, -4.64) * mm, v(18.3, -4.67) * mm]});
            skFitSpline(sketch, "E69.0", {"points": [v(13.02, -3.33) * mm, v(13.77, -4.16) * mm, v(14.52, -5) * mm, v(15.27, -5.84) * mm]});
            skFitSpline(sketch, "E70", {"points": [v(1.26, 13.28) * mm, v(-1.41, 16.52) * mm], "startDerivative": vector(-2.65, 3.22) * mm, "endDerivative": vector(-2.65, 3.22) * mm});
            skFitSpline(sketch, "E71", {"points": [v(-1.41, 16.52) * mm, v(-1.09, 17.86) * mm, v(-0.8, 19.78) * mm, v(-1.18, 21.56) * mm, v(-2, 22.24) * mm, v(-2.66, 21.59) * mm, v(-2.6, 20.1) * mm, v(-2.6, 19.1) * mm], "startDerivative": vector(2.2, 8.8) * mm, "endDerivative": vector(-0.5, -7.6) * mm});
            skFitSpline(sketch, "E72", {"points": [v(-0.15, 12.12) * mm, v(-2.1, 14.42) * mm], "startDerivative": vector(-1.97, 2.39) * mm, "endDerivative": vector(-1.97, 2.39) * mm});
            skFitSpline(sketch, "E73", {"points": [v(-2.1, 14.42) * mm, v(-2.75, 13.6) * mm, v(-3.63, 12.94) * mm, v(-4.79, 12.8) * mm, v(-4.85, 13.7) * mm, v(-3.58, 14.83) * mm, v(-2.92, 15.55) * mm], "startDerivative": vector(-3.9, -5.4) * mm, "endDerivative": vector(3.42, 4.58) * mm});
            skFitSpline(sketch, "E74.0", {"points": [v(1.85, 13.77) * mm, v(0.96, 14.84) * mm, v(0.06, 15.94) * mm, v(-0.82, 17) * mm]});
            skFitSpline(sketch, "E75.0", {"points": [v(-0.68, 16.34) * mm, v(-0.64, 16.52) * mm, v(-0.54, 16.9) * mm, v(-0.42, 17.38) * mm, v(-0.32, 17.8) * mm, v(-0.22, 18.27) * mm, v(-0.1, 18.9) * mm, v(-0.03, 19.58) * mm, v(-0.04, 20.15) * mm, v(-0.08, 20.56) * mm, v(-0.15, 20.98) * mm, v(-0.27, 21.38) * mm, v(-0.43, 21.78) * mm, v(-0.64, 22.15) * mm, v(-0.9, 22.49) * mm, v(-1.2, 22.74) * mm, v(-1.48, 22.9) * mm, v(-1.7, 22.96) * mm, v(-1.9, 23) * mm, v(-2.1, 23) * mm, v(-2.34, 22.95) * mm, v(-2.6, 22.84) * mm, v(-2.88, 22.65) * mm, v(-3.14, 22.35) * mm, v(-3.32, 22) * mm, v(-3.41, 21.68) * mm, v(-3.46, 21.38) * mm, v(-3.47, 21.03) * mm, v(-3.43, 20.65) * mm, v(-3.4, 20.36) * mm, v(-3.36, 20.17) * mm, v(-3.35, 20.04) * mm, v(-3.34, 19.92) * mm, v(-3.33, 19.77) * mm, v(-3.33, 19.6) * mm, v(-3.33, 19.38) * mm, v(-3.34, 19.23) * mm, v(-3.35, 19.15) * mm]});
            skFitSpline(sketch, "E76.0", {"points": [v(-0.74, 11.63) * mm, v(-1.39, 12.41) * mm, v(-2.02, 13.12) * mm, v(-2.69, 13.93) * mm]});
            skFitSpline(sketch, "E77.0", {"points": [v(-1.47, 13.97) * mm, v(-1.55, 13.86) * mm, v(-1.72, 13.63) * mm, v(-2, 13.27) * mm, v(-2.32, 12.91) * mm, v(-2.65, 12.63) * mm, v(-2.95, 12.43) * mm, v(-3.2, 12.3) * mm, v(-3.48, 12.17) * mm, v(-3.78, 12.06) * mm, v(-4.1, 11.97) * mm, v(-4.4, 11.94) * mm, v(-4.66, 11.95) * mm, v(-4.88, 11.99) * mm, v(-5.1, 12.08) * mm, v(-5.34, 12.24) * mm, v(-5.51, 12.43) * mm, v(-5.67, 12.72) * mm, v(-5.75, 13.07) * mm, v(-5.74, 13.47) * mm, v(-5.65, 13.8) * mm, v(-5.54, 14.04) * mm, v(-5.4, 14.28) * mm, v(-5.2, 14.53) * mm, v(-4.95, 14.77) * mm, v(-4.7, 14.97) * mm, v(-4.45, 15.14) * mm, v(-4.23, 15.3) * mm, v(-4.09, 15.4) * mm, v(-4, 15.48) * mm, v(-3.88, 15.58) * mm, v(-3.73, 15.74) * mm, v(-3.6, 15.9) * mm, v(-3.54, 16) * mm]});
            skFitSpline(sketch, "E78", {"points": [v(-2.92, 15.55) * mm, v(-5.53, 15.55) * mm, v(-6.93, 16.43) * mm, v(-6.86, 17.3) * mm, v(-5.2, 17.13) * mm, v(-3.68, 17.01) * mm], "startDerivative": vector(-10.75, -1.04) * mm, "endDerivative": vector(7.27, -0.04) * mm});
            skFitSpline(sketch, "E79.0", {"points": [v(-2.85, 14.8) * mm, v(-3.08, 14.78) * mm, v(-3.53, 14.73) * mm, v(-4.23, 14.69) * mm, v(-4.94, 14.7) * mm, v(-5.65, 14.78) * mm, v(-6.35, 15) * mm, v(-6.87, 15.28) * mm, v(-7.24, 15.6) * mm, v(-7.48, 15.88) * mm, v(-7.67, 16.23) * mm, v(-7.78, 16.6) * mm, v(-7.8, 16.99) * mm, v(-7.74, 17.34) * mm, v(-7.58, 17.63) * mm, v(-7.41, 17.83) * mm, v(-7.18, 18) * mm, v(-6.95, 18.08) * mm, v(-6.74, 18.12) * mm, v(-6.48, 18.13) * mm, v(-6.19, 18.1) * mm, v(-5.86, 18.05) * mm, v(-5.55, 17.98) * mm, v(-5.3, 17.92) * mm, v(-5.12, 17.88) * mm, v(-4.96, 17.85) * mm, v(-4.76, 17.82) * mm, v(-4.47, 17.78) * mm, v(-4.11, 17.76) * mm, v(-3.82, 17.76) * mm, v(-3.67, 17.76) * mm]});
            skFitSpline(sketch, "E80", {"points": [v(-2.6, 19.1) * mm, v(-4, 20.95) * mm, v(-5.34, 21.83) * mm, v(-6.18, 21.52) * mm, v(-6.45, 20.42) * mm, v(-5.1, 18.6) * mm, v(-3.68, 17.01) * mm], "startDerivative": vector(-6.76, 10.07) * mm, "endDerivative": vector(7.14, -8.19) * mm});
            skFitSpline(sketch, "E81.0", {"points": [v(-1.97, 19.52) * mm, v(-2.11, 19.73) * mm, v(-2.4, 20.15) * mm, v(-2.86, 20.8) * mm, v(-3.37, 21.4) * mm, v(-3.85, 21.87) * mm, v(-4.28, 22.19) * mm, v(-4.63, 22.39) * mm, v(-5.01, 22.54) * mm, v(-5.45, 22.6) * mm, v(-5.89, 22.56) * mm, v(-6.42, 22.35) * mm, v(-6.84, 21.97) * mm, v(-7.1, 21.47) * mm, v(-7.23, 21.05) * mm, v(-7.25, 20.67) * mm, v(-7.21, 20.36) * mm, v(-7.13, 20.05) * mm, v(-6.98, 19.7) * mm, v(-6.74, 19.33) * mm, v(-6.48, 18.98) * mm, v(-6.2, 18.66) * mm, v(-5.91, 18.36) * mm, v(-5.64, 18.08) * mm, v(-5.4, 17.8) * mm, v(-5.07, 17.46) * mm, v(-4.69, 17.03) * mm, v(-4.4, 16.69) * mm, v(-4.24, 16.52) * mm]});
            skPoint(sketch, "E82", {"position": v(11.48, 16.02) * mm});
            skPoint(sketch, "E83", {"position": v(15.2, 17.66) * mm});
            skPoint(sketch, "E84", {"position": v(22.41, 8.87) * mm});
            skPoint(sketch, "E85", {"position": v(21.75, 5.72) * mm});
            skPoint(sketch, "E86", {"position": v(13.22, 16.86) * mm});
            skPoint(sketch, "E87", {"position": v(12.79, 14.76) * mm});
            skPoint(sketch, "E88", {"position": v(15.92, 11.6) * mm});
            skPoint(sketch, "E89", {"position": v(19, 8.5) * mm});
            skPoint(sketch, "E90", {"position": v(21.02, 8.75) * mm});
            skPoint(sketch, "E91", {"position": v(19, 10.24) * mm});
            skPoint(sketch, "E92", {"position": v(18.1, 11.33) * mm});
            skPoint(sketch, "E93", {"position": v(15.74, 13.62) * mm});
            skPoint(sketch, "E94", {"position": v(15.01, 16.45) * mm});
            skPoint(sketch, "E95", {"position": v(22.31, 8.02) * mm});
            skPoint(sketch, "E96", {"position": v(22, 6.6) * mm});
            skPoint(sketch, "E97", {"position": v(15, 14.9) * mm});
            skFitSpline(sketch, "E98", {"points": [v(21.75, 5.72) * mm, v(19, 8.5) * mm, v(15.92, 11.6) * mm, v(12.79, 14.76) * mm, v(11.48, 16.02) * mm, v(13.22, 16.86) * mm, v(15.2, 17.66) * mm, v(15.01, 16.45) * mm, v(15, 14.9) * mm, v(15.74, 13.62) * mm, v(18.1, 11.33) * mm, v(19, 10.24) * mm, v(21.02, 8.75) * mm, v(22.41, 8.87) * mm, v(22.31, 8.02) * mm, v(22, 6.6) * mm, v(21.75, 5.72) * mm]});
            skLineSegment(sketch, "E99", {"start": v(14.76, -8.13) * mm, "end": v(15.28, -7.55) * mm});
            skLineSegment(sketch, "E100", {"start": v(19.49, -10.52) * mm, "end": v(19.79, -9.82) * mm});
            skLineSegment(sketch, "E101", {"start": v(22.65, -6.97) * mm, "end": v(22.1, -6.43) * mm});
            skLineSegment(sketch, "E102", {"start": v(14.6, -1.7) * mm, "end": v(15.12, -1.15) * mm});
            skLineSegment(sketch, "E103", {"start": v(12.43, -4.08) * mm, "end": v(13.07, -3.38) * mm});
            skLineSegment(sketch, "E104", {"start": v(13.07, -3.38) * mm, "end": v(13.59, -2.81) * mm});
            skLineSegment(sketch, "E105", {"start": v(13.59, -2.81) * mm, "end": v(14.6, -1.7) * mm});
            skLineSegment(sketch, "E106", {"start": v(15.12, -1.15) * mm, "end": v(15.43, -0.8) * mm});
            skLineSegment(sketch, "E107", {"start": v(15.12, -1.15) * mm, "end": v(17.31, -3.3) * mm});
            skLineSegment(sketch, "E108", {"start": v(18.42, -5.43) * mm, "end": v(20.76, -4.14) * mm});
            skLineSegment(sketch, "E109", {"start": v(17.4, -4.46) * mm, "end": v(17.31, -3.3) * mm});
            skPoint(sketch, "E110", {"position": v(17.64, -2.96) * mm});
            skPoint(sketch, "E111", {"position": v(18.38, -2.39) * mm});
            skPoint(sketch, "E112", {"position": v(19.27, -2) * mm});
            skPoint(sketch, "E113", {"position": v(20.44, -2.17) * mm});
            skPoint(sketch, "E114", {"position": v(20.88, -2.76) * mm});
            skPoint(sketch, "E115", {"position": v(20.94, -3.5) * mm});
            skFitSpline(sketch, "E116", {"points": [v(17.31, -3.3) * mm, v(17.64, -2.96) * mm, v(18.38, -2.39) * mm, v(19.27, -2) * mm, v(20.44, -2.17) * mm, v(20.88, -2.76) * mm, v(20.94, -3.5) * mm, v(20.76, -4.14) * mm], "startDerivative": vector(2.6, 2.92) * mm, "endDerivative": vector(-1.7, -4.75) * mm});
            skSolve(sketch);
        }
        {
            var Q0;
            Q0=makeQuery(id+"F0.imprint","IMPRINT",FACE,{"disambiguationData":[TD([[makeQuery(id+"F0.imprint","IMPRINT",EDGE,{"derivedFrom":sQuery(id+"F0.wireOp",EDGE,"E2.0")}),-1.0]])]});
            var Q1;
            {var subQ1=sQuery(id+"F0.wireOp",EDGE,"E70");Q1=makeQuery(id+"F0.imprint","IMPRINT",FACE,{"disambiguationData":[TD([[makeQuery(id+"F0.imprint","IMPRINT",EDGE,{"derivedFrom":subQ1}),1.0]])]});}
            var Q2;
            Q2=makeQuery(id+"F0.imprint","IMPRINT",FACE,{"disambiguationData":[TD([[makeQuery(id+"F0.imprint","IMPRINT",EDGE,{"derivedFrom":sQuery(id+"F0.wireOp",EDGE,"E47")}),1.0]])]});
            var Q3;
            {var subQ4=sQuery(id+"F0.wireOp",EDGE,"E43.0");Q3=makeQuery(id+"F0.imprint","IMPRINT",FACE,{"disambiguationData":[TD([[makeQuery(id+"F0.imprint","IMPRINT",EDGE,{"derivedFrom":subQ4}),1.0]])]});}
            var Q4;
            {var subQ0=sQuery(id+"F0.wireOp",EDGE,"E60");Q4=makeQuery(id+"F0.imprint","IMPRINT",FACE,{"disambiguationData":[TD([[makeQuery(id+"F0.imprint","IMPRINT",EDGE,{"derivedFrom":subQ0}),1.0]])]});}
            var Q5;
            Q5=makeQuery(id+"F0.imprint","IMPRINT",FACE,{"disambiguationData":[TD([[makeQuery(id+"F0.imprint","IMPRINT",EDGE,{"derivedFrom":sQuery(id+"F0.wireOp",EDGE,"E51.0")}),1.0]])]});
            var Q6;
            Q6=makeQuery(id+"F0.imprint","IMPRINT",FACE,{"disambiguationData":[TD([[makeQuery(id+"F0.imprint","IMPRINT",EDGE,{"derivedFrom":sQuery(id+"F0.wireOp",EDGE,"E98")}),-1.0]])]});
            extrude(context, id + "F1", {"entities" : qUnion([Q0, Q1, Q2, Q3, Q4, Q5, Q6]), "depth" : 1.27 * mm});
        }
        {
            var Q0;
            Q0=makeQuery(id+"F0.imprint","IMPRINT",FACE,{"disambiguationData":[TD([[makeQuery(id+"F0.imprint","IMPRINT",EDGE,{"derivedFrom":sQuery(id+"F0.wireOp",EDGE,"E1")}),-1.0]])]});
            var Q1;
            {var subQ11=sQuery(id+"F0.wireOp",EDGE,"E70");Q1=makeQuery(id+"F0.imprint","IMPRINT",FACE,{"disambiguationData":[TD([[makeQuery(id+"F0.imprint","IMPRINT",EDGE,{"derivedFrom":subQ11}),-1.0]])]});}
            var Q2;
            {var subQ8=sQuery(id+"F0.wireOp",EDGE,"E60");Q2=makeQuery(id+"F0.imprint","IMPRINT",FACE,{"disambiguationData":[TD([[makeQuery(id+"F0.imprint","IMPRINT",EDGE,{"derivedFrom":subQ8}),-1.0]])]});}
            var Q3;
            {var subQ3=sQuery(id+"F0.wireOp",EDGE,"E101");Q3=makeQuery(id+"F0.imprint","IMPRINT",FACE,{"disambiguationData":[TD([[makeQuery(id+"F0.imprint","IMPRINT",EDGE,{"derivedFrom":subQ3}),1.0]])]});}
            var Q4;
            {var subQ0=sQuery(id+"F0.wireOp",EDGE,"E101");Q4=makeQuery(id+"F0.imprint","IMPRINT",FACE,{"disambiguationData":[TD([[makeQuery(id+"F0.imprint","IMPRINT",EDGE,{"derivedFrom":subQ0}),-1.0]])]});}
            var Q5;
            Q5=makeQuery(id+"F0.imprint","IMPRINT",FACE,{"disambiguationData":[TD([[makeQuery(id+"F0.imprint","IMPRINT",EDGE,{"derivedFrom":sQuery(id+"F0.wireOp",EDGE,"E65")}),-1.0]])]});
            var Q6;
            Q6=makeQuery(id+"F0.imprint","IMPRINT",FACE,{"disambiguationData":[TD([[makeQuery(id+"F0.imprint","IMPRINT",EDGE,{"derivedFrom":sQuery(id+"F0.wireOp",EDGE,"E64")}),-1.0]])]});
            var Q7;
            Q7=makeQuery(id+"F0.imprint","IMPRINT",FACE,{"disambiguationData":[TD([[makeQuery(id+"F0.imprint","IMPRINT",EDGE,{"derivedFrom":sQuery(id+"F0.wireOp",EDGE,"E27")}),1.0]])]});
            var Q8;
            Q8=makeQuery(id+"F0.imprint","IMPRINT",FACE,{"disambiguationData":[TD([[makeQuery(id+"F0.imprint","IMPRINT",EDGE,{"derivedFrom":sQuery(id+"F0.wireOp",EDGE,"E28")}),1.0]])]});
            var Q9;
            Q9=makeQuery(id+"F0.imprint","IMPRINT",FACE,{"disambiguationData":[TD([[makeQuery(id+"F0.imprint","IMPRINT",EDGE,{"derivedFrom":sQuery(id+"F0.wireOp",EDGE,"E23")}),1.0]])]});
            var Q10;
            Q10=makeQuery(id+"F0.imprint","IMPRINT",FACE,{"disambiguationData":[TD([[makeQuery(id+"F0.imprint","IMPRINT",EDGE,{"derivedFrom":sQuery(id+"F0.wireOp",EDGE,"E29")}),-1.0]])]});
            extrude(context, id + "F2", {"entities" : qUnion([Q0, Q1, Q2, Q3, Q4, Q5, Q6, Q7, Q8, Q9, Q10]), "depth" : 2.3 * mm});
        }
    });
